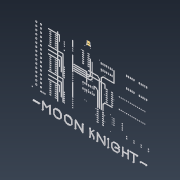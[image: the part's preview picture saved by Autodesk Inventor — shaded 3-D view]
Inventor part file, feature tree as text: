
AUTODESK INVENTOR PART (.ipt)
format: ipt  version: 2022.3 (Build 263350000, 350)  size: 4,884,480 bytes
history: mixed  units: in
note: dims shown in document units (in); Inventor stores cm internally (conversion verified against a paired STEP export)
features: other x297, projected_geometry x12, extrude x1, fillet x1, sketch x1, imported_body x1
ambient origin geometry x8: Origin, YZ Plane, XZ Plane, XY Plane, X Axis, Y Axis, Z Axis, Center Point
bodies: Solid1 (imported_parasolid), Solid2 (imported_parasolid), Solid3 (imported_parasolid), Solid4 (imported_parasolid), Solid5 (imported_parasolid), Solid6 (imported_parasolid), Solid7 (imported_parasolid), Solid8 (imported_parasolid), Solid9 (imported_parasolid), Solid10 (imported_parasolid), Solid11 (imported_parasolid), Solid12 (imported_parasolid), Solid13 (imported_parasolid), Solid14 (imported_parasolid), Solid15 (imported_parasolid), Solid16 (imported_parasolid), Solid17 (imported_parasolid), Solid18 (imported_parasolid), Solid19 (imported_parasolid), Solid20 (imported_parasolid), Solid21 (imported_parasolid), Solid22 (imported_parasolid), Solid23 (imported_parasolid), Solid24 (imported_parasolid), Solid25 (imported_parasolid), Solid26 (imported_parasolid), Solid27 (imported_parasolid), Solid28 (imported_parasolid), Solid29 (imported_parasolid), Solid30 (imported_parasolid), Solid31 (imported_parasolid), Solid32 (imported_parasolid), Solid33 (imported_parasolid), Solid34 (imported_parasolid), Solid35 (imported_parasolid), Solid36 (imported_parasolid), Solid37 (imported_parasolid), Solid38 (imported_parasolid), Solid39 (imported_parasolid), Solid40 (imported_parasolid), Solid41 (imported_parasolid), Solid42 (imported_parasolid), Solid43 (imported_parasolid), Solid44 (imported_parasolid), Solid45 (imported_parasolid), Solid46 (imported_parasolid), Solid47 (imported_parasolid), Solid48 (imported_parasolid), Solid49 (imported_parasolid), Solid50 (imported_parasolid), Solid51 (imported_parasolid), Solid52 (imported_parasolid), Solid53 (imported_parasolid), Solid54 (imported_parasolid), Solid55 (imported_parasolid), Solid56 (imported_parasolid), Solid57 (imported_parasolid), Solid58 (imported_parasolid), Solid59 (imported_parasolid), Solid60 (imported_parasolid), Solid61 (imported_parasolid), Solid62 (imported_parasolid), Solid63 (imported_parasolid), Solid64 (imported_parasolid), Solid65 (imported_parasolid), Solid66 (imported_parasolid), Solid67 (imported_parasolid), Solid68 (imported_parasolid), Solid69 (imported_parasolid), Solid70 (imported_parasolid), Solid71 (imported_parasolid), Solid72 (imported_parasolid), Solid73 (imported_parasolid), Solid74 (imported_parasolid), Solid75 (imported_parasolid), Solid76 (imported_parasolid), Solid77 (imported_parasolid), Solid78 (imported_parasolid), Solid79 (imported_parasolid), Solid80 (imported_parasolid), Solid81 (imported_parasolid), Solid82 (imported_parasolid), Solid83 (imported_parasolid), Solid84 (imported_parasolid), Solid85 (imported_parasolid), Solid86 (imported_parasolid), Solid87 (imported_parasolid), Solid88 (imported_parasolid), Solid89 (imported_parasolid), Solid90 (imported_parasolid), Solid91 (imported_parasolid), Solid92 (imported_parasolid), Solid93 (imported_parasolid), Solid94 (imported_parasolid), Solid95 (imported_parasolid), Solid96 (imported_parasolid), Solid97 (imported_parasolid), Solid98 (imported_parasolid), Solid99 (imported_parasolid), Solid100 (imported_parasolid), Solid101 (imported_parasolid), Solid102 (imported_parasolid), Solid103 (imported_parasolid), Solid104 (imported_parasolid), Solid105 (imported_parasolid), Solid106 (imported_parasolid), Solid107 (imported_parasolid), Solid108 (imported_parasolid), Solid109 (imported_parasolid), Solid110 (imported_parasolid), Solid111 (imported_parasolid), Solid112 (imported_parasolid), Solid113 (imported_parasolid), Solid114 (imported_parasolid), Solid115 (imported_parasolid), Solid116 (imported_parasolid), Solid117 (imported_parasolid), Solid118 (imported_parasolid), Solid119 (imported_parasolid), Solid120 (imported_parasolid), Solid121 (imported_parasolid), Solid122 (imported_parasolid), Solid123 (imported_parasolid), Solid124 (imported_parasolid), Solid125 (imported_parasolid), Solid126 (imported_parasolid), Solid127 (imported_parasolid), Solid128 (imported_parasolid), Solid129 (imported_parasolid), Solid130 (imported_parasolid), Solid131 (imported_parasolid), Solid132 (imported_parasolid), Solid133 (imported_parasolid), Solid134 (imported_parasolid), Solid135 (imported_parasolid), Solid136 (imported_parasolid), Solid137 (imported_parasolid), Solid138 (imported_parasolid), Solid139 (imported_parasolid), Solid140 (imported_parasolid), Solid141 (imported_parasolid), Solid142 (imported_parasolid), Solid143 (imported_parasolid), Solid144 (imported_parasolid), Solid145 (imported_parasolid), Solid146 (imported_parasolid), Solid147 (imported_parasolid), Solid148 (imported_parasolid), Solid149 (imported_parasolid), Solid150 (imported_parasolid), Solid151 (imported_parasolid), Solid152 (imported_parasolid), Solid153 (imported_parasolid), Solid154 (imported_parasolid), Solid155 (imported_parasolid), Solid156 (imported_parasolid), Solid157 (imported_parasolid), Solid158 (imported_parasolid), Solid159 (imported_parasolid), Solid160 (imported_parasolid), Solid161 (imported_parasolid), Solid162 (imported_parasolid), Solid163 (imported_parasolid), Solid164 (imported_parasolid), Solid165 (imported_parasolid), Solid166 (imported_parasolid), Solid167 (imported_parasolid), Solid168 (imported_parasolid), Solid169 (imported_parasolid), Solid170 (imported_parasolid), Solid171 (imported_parasolid), Solid172 (imported_parasolid), Solid173 (imported_parasolid), Solid174 (imported_parasolid), Solid175 (imported_parasolid), Solid176 (imported_parasolid), Solid177 (imported_parasolid), Solid178 (imported_parasolid), Solid179 (imported_parasolid), Solid180 (imported_parasolid), Solid181 (imported_parasolid), Solid182 (imported_parasolid), Solid183 (imported_parasolid), Solid184 (imported_parasolid), Solid185 (imported_parasolid), Solid186 (imported_parasolid), Solid187 (imported_parasolid), Solid188 (imported_parasolid), Solid189 (imported_parasolid), Solid190 (imported_parasolid), Solid191 (imported_parasolid), Solid192 (imported_parasolid), Solid193 (imported_parasolid), Solid194 (imported_parasolid), Solid195 (imported_parasolid), Solid196 (imported_parasolid), Solid197 (imported_parasolid), Solid198 (imported_parasolid), Solid199 (imported_parasolid), Solid200 (imported_parasolid), Solid201 (imported_parasolid), Solid202 (imported_parasolid), Solid203 (imported_parasolid), Solid204 (imported_parasolid), Solid205 (imported_parasolid), Solid206 (imported_parasolid), Solid207 (imported_parasolid), Solid208 (imported_parasolid), Solid209 (imported_parasolid), Solid210 (imported_parasolid), Solid211 (imported_parasolid), Solid212 (imported_parasolid), Solid213 (imported_parasolid), Solid214 (imported_parasolid), Solid215 (imported_parasolid), Solid216 (imported_parasolid), Solid217 (imported_parasolid), Solid218 (imported_parasolid), Solid219 (imported_parasolid), Solid220 (imported_parasolid), Solid221 (imported_parasolid), Solid222 (imported_parasolid), Solid223 (imported_parasolid), Solid224 (imported_parasolid), Solid225 (imported_parasolid), Solid226 (imported_parasolid), Solid227 (imported_parasolid), Solid228 (imported_parasolid), Solid229 (imported_parasolid), Solid230 (imported_parasolid), Solid231 (imported_parasolid), Solid232 (imported_parasolid), Solid233 (imported_parasolid), Solid234 (imported_parasolid), Solid235 (imported_parasolid), Solid236 (imported_parasolid), Solid237 (imported_parasolid), Solid238 (imported_parasolid), Solid239 (imported_parasolid), Solid240 (imported_parasolid), Solid241 (imported_parasolid), Solid242 (imported_parasolid), Solid243 (imported_parasolid), Solid244 (imported_parasolid), Solid245 (imported_parasolid), Solid246 (imported_parasolid), Solid247 (imported_parasolid), Solid248 (imported_parasolid), Solid249 (imported_parasolid), Solid250 (imported_parasolid), Solid251 (imported_parasolid), Solid252 (imported_parasolid), Solid253 (imported_parasolid), Solid254 (imported_parasolid), Solid255 (imported_parasolid), Solid256 (imported_parasolid), Solid257 (imported_parasolid), Solid258 (imported_parasolid), Solid259 (imported_parasolid), Solid260 (imported_parasolid), Solid261 (imported_parasolid), Solid262 (imported_parasolid), Solid263 (imported_parasolid), Solid264 (imported_parasolid), Solid265 (imported_parasolid), Solid266 (imported_parasolid), Solid267 (imported_parasolid), Solid268 (imported_parasolid), Solid269 (imported_parasolid), Solid270 (imported_parasolid), Solid271 (imported_parasolid), Solid272 (imported_parasolid), Solid273 (imported_parasolid), Solid274 (imported_parasolid), Solid275 (imported_parasolid), Solid276 (imported_parasolid), Solid277 (imported_parasolid), Solid278 (imported_parasolid), Solid279 (imported_parasolid), Solid280 (imported_parasolid), Solid281 (imported_parasolid), Solid282 (imported_parasolid), Solid283 (imported_parasolid), Solid284 (imported_parasolid), Solid285 (imported_parasolid), Solid286 (imported_parasolid), Solid287 (imported_parasolid), Solid288 (imported_parasolid), Solid289 (imported_parasolid), Solid290 (imported_parasolid), Solid291 (imported_parasolid), Solid292 (imported_parasolid), Solid293 (imported_parasolid), Solid294 (imported_parasolid), Solid295 (imported_parasolid), Solid296 (imported_parasolid), Solid297 (imported_parasolid), Solid298 (imported_parasolid), Solid299 (imported_parasolid), Body1 (imported_parasolid), Body3 (imported_parasolid)
feature tree (313):
  extrude  "Extrusion1"  Depth=0.0197in
  fillet  "Fillet1"  [1 undecoded]
  sketch  "Sketch1"  dims[d0=0.0394in d1=0.0in d2=0.0197in]
  projected_geometry  "Projected Loop1"
  projected_geometry  "Projected Loop2"
  projected_geometry  "Projected Loop3"
  projected_geometry  "Projected Loop4"
  projected_geometry  "Projected Loop5"
  projected_geometry  "Projected Loop6"
  projected_geometry  "Projected Loop7"
  projected_geometry  "Projected Loop8"
  projected_geometry  "Projected Loop9"
  projected_geometry  "Projected Loop10"
  projected_geometry  "Projected Loop11"
  projected_geometry  "Projected Loop12"
  other  "Body1:1"
  other  "Body1:2"
  other  "Body1:3"
  other  "Body1:4"
  other  "Body1:5"
  other  "Body1:6"
  other  "Body1:7"
  other  "Body1:8"
  other  "Body1:9"
  other  "Body1:10"
  other  "Body1:11"
  other  "Body1:12"
  other  "Body1:13"
  other  "Body1:14"
  other  "Body1:15"
  other  "Body1:16"
  other  "Body1:17"
  other  "Body1:18"
  other  "Body1:19"
  other  "Body1:20"
  other  "Body1:21"
  other  "Body1:22"
  other  "Body1:23"
  other  "Body1:24"
  other  "Body1:25"
  other  "Body1:26"
  other  "Body1:27"
  other  "Body1:28"
  other  "Body1:29"
  other  "Body1:30"
  other  "Body1:31"
  other  "Body1:32"
  other  "Body1:33"
  other  "Body1:34"
  other  "Body1:35"
  other  "Body1:36"
  other  "Body1:37"
  other  "Body1:38"
  other  "Body1:39"
  other  "Body1:40"
  other  "Body1:41"
  other  "Body1:42"
  other  "Body1:43"
  other  "Body1:44"
  other  "Body1:45"
  other  "Body1:46"
  other  "Body1:47"
  other  "Body1:48"
  other  "Body1:49"
  other  "Body1:50"
  other  "Body1:51"
  other  "Body1:52"
  other  "Body1:53"
  other  "Body1:54"
  other  "Body1:55"
  other  "Body1:56"
  other  "Body1:57"
  other  "Body1:58"
  other  "Body1:59"
  other  "Body1:60"
  other  "Body1:61"
  other  "Body1:62"
  other  "Body1:63"
  other  "Body1:64"
  other  "Body1:65"
  other  "Body1:66"
  other  "Body1:67"
  other  "Body1:68"
  other  "Body1:69"
  other  "Body1:70"
  other  "Body1:71"
  other  "Body1:72"
  other  "Body1:73"
  other  "Body1:74"
  other  "Body1:75"
  other  "Body1:76"
  other  "Body1:77"
  other  "Body1:78"
  other  "Body1:79"
  other  "Body1:80"
  other  "Body1:81"
  other  "Body1:82"
  other  "Body1:83"
  other  "Body1:84"
  other  "Body1:85"
  other  "Body1:86"
  other  "Body1:87"
  other  "Body1:88"
  other  "Body1:89"
  other  "Body1:90"
  other  "Body1:91"
  other  "Body1:92"
  other  "Body1:93"
  other  "Body1:94"
  other  "Body1:95"
  other  "Body1:96"
  other  "Body1:97"
  other  "Body1:98"
  other  "Body1:99"
  other  "Body1:100"
  other  "Body1:101"
  other  "Body1:102"
  other  "Body1:103"
  other  "Body1:104"
  other  "Body1:105"
  other  "Body1:106"
  other  "Body1:107"
  other  "Body1:108"
  other  "Body1:109"
  other  "Body1:110"
  other  "Body1:111"
  other  "Body1:112"
  other  "Body1:113"
  other  "Body1:114"
  other  "Body1:115"
  other  "Body1:116"
  other  "Body1:117"
  other  "Body1:118"
  other  "Body1:119"
  other  "Body1:120"
  other  "Body1:121"
  other  "Body1:122"
  other  "Body1:123"
  other  "Body1:124"
  other  "Body1:125"
  other  "Body1:126"
  other  "Body1:127"
  other  "Body1:128"
  other  "Body1:129"
  other  "Body1:130"
  other  "Body1:131"
  other  "Body1:132"
  other  "Body1:133"
  other  "Body1:134"
  other  "Body1:135"
  other  "Body1:136"
  other  "Body1:137"
  other  "Body1:138"
  other  "Body1:139"
  other  "Body1:140"
  other  "Body1:141"
  other  "Body1:142"
  other  "Body1:143"
  other  "Body1:144"
  other  "Body1:145"
  other  "Body1:146"
  other  "Body1:147"
  other  "Body1:148"
  other  "Body1:149"
  other  "Body1:150"
  other  "Body1:151"
  other  "Body1:152"
  other  "Body1:153"
  other  "Body1:154"
  other  "Body1:155"
  other  "Body1:156"
  other  "Body1:157"
  other  "Body1:158"
  other  "Body1:159"
  other  "Body1:160"
  other  "Body1:161"
  other  "Body1:162"
  other  "Body1:163"
  other  "Body1:164"
  other  "Body1:165"
  other  "Body1:166"
  other  "Body1:167"
  other  "Body1:168"
  other  "Body1:169"
  other  "Body1:170"
  other  "Body1:171"
  other  "Body1:172"
  other  "Body1:173"
  other  "Body1:174"
  other  "Body1:175"
  other  "Body1:176"
  other  "Body1:177"
  other  "Body1:178"
  other  "Body1:179"
  other  "Body1:180"
  other  "Body1:181"
  other  "Body1:182"
  other  "Body1:183"
  other  "Body1:184"
  other  "Body1:185"
  other  "Body1:186"
  other  "Body1:187"
  other  "Body1:188"
  other  "Body1:189"
  other  "Body1:190"
  other  "Body1:191"
  other  "Body1:192"
  other  "Body1:193"
  other  "Body1:194"
  other  "Body1:195"
  other  "Body1:196"
  other  "Body1:197"
  other  "Body1:198"
  other  "Body1:199"
  other  "Body1:200"
  other  "Body1:201"
  other  "Body1:202"
  other  "Body1:203"
  other  "Body1:204"
  other  "Body1:205"
  other  "Body1:206"
  other  "Body1:207"
  other  "Body1:208"
  other  "Body1:209"
  other  "Body1:210"
  other  "Body1:211"
  other  "Body1:212"
  other  "Body1:213"
  other  "Body1:214"
  other  "Body1:215"
  other  "Body1:216"
  other  "Body1:217"
  other  "Body1:218"
  other  "Body1:219"
  other  "Body1:220"
  other  "Body1:221"
  other  "Body1:222"
  other  "Body1:223"
  other  "Body1:224"
  other  "Body1:225"
  other  "Body1:226"
  other  "Body1:227"
  other  "Body1:228"
  other  "Body1:229"
  other  "Body1:230"
  other  "Body1:231"
  other  "Body1:232"
  other  "Body1:233"
  other  "Body1:234"
  other  "Body1:235"
  other  "Body1:236"
  other  "Body1:237"
  other  "Body1:238"
  other  "Body1:239"
  other  "Body1:240"
  other  "Body1:241"
  other  "Body1:242"
  other  "Body1:243"
  other  "Body1:244"
  other  "Body1:245"
  other  "Body1:246"
  other  "Body1:247"
  other  "Body1:248"
  other  "Body1:249"
  other  "Body1:250"
  other  "Body1:251"
  other  "Body1:252"
  other  "Body1:253"
  other  "Body1:254"
  other  "Body1:255"
  other  "Body1:256"
  other  "Body1:257"
  other  "Body1:258"
  other  "Body1:259"
  other  "Body1:260"
  other  "Body1:261"
  other  "Body1:262"
  other  "Body1:263"
  other  "Body1:264"
  other  "Body1:265"
  other  "Body1:266"
  other  "Body1:267"
  other  "Body1:268"
  other  "Body1:269"
  other  "Body1:270"
  other  "Body1:271"
  other  "Body1:272"
  other  "Body1:273"
  other  "Body1:274"
  other  "Body1:275"
  other  "Body1:276"
  other  "Body1:277"
  other  "Body1:278"
  other  "Body1:279"
  other  "Body1:280"
  other  "Body1:281"
  other  "Body1:282"
  other  "Body1:283"
  other  "Body1:284"
  other  "Body1:285"
  other  "Body1:286"
  other  "Body1:287"
  other  "Body1:288"
  other  "Body1:289"
  other  "Body1:290"
  other  "Body1:291"
  other  "Body1:292"
  other  "Body1:293"
  other  "Body1:294"
  other  "Body1:295"
  other  "Body1:296"
  other  "Body1:297"
  imported_body  NMx_Import_Brep_tag  [imported B-rep: ~2135 faces, bbox_mm=[163.09413, 115.165, 1.035]]
note: 1 required parameter value undecoded (feature->parameter linkage not recoverable at this tier; creation-order binding heuristic only, values carry confidence <= 0.55)
